# Revit family: Shower-Thermostat_Mixer-GROHE-Euphoria-26177_Series
name_source: partatom
category: Plumbing Fixtures
revit_build: Autodesk Revit 2014 (Build: 20130308_1515(x64)
units: mm (PartAtom-declared; Revit-internal decimal feet)

## types (2) — shared parameters
Assembly Code = D2010710
CW Connection = Yes
CWFU = 3
Cold Water Connection Diameter = 1/2"
Default Elevation = 40"
Description = EUPHORIA SYSTEM 260 Shower System with Bath Thermostat for Wall Mount
Finish = Metal-Grohe-000-Chrome
HW Connection = Yes
HWFU = 3
Height = 2 3/4"
Hot Water Connection Diameter = 1"
Installation Type = Wall Mounted
Manufacturer = Grohe
Material = Metal-Grohe-000-Chrome
Price = Prices may vary. Please consult Manufacturer Representative for most up-to-date price list.
Product Page URL = https://www.grohe.ca
Tempered Connection Diameter = 1/2"
URL = https://www.grohe.us
Vent Connection = No
WFU = 4
Warranty Documentation Link = https://cdn.cloud.grohe.com
Waste Connection = No
Width = 11 3/4"

## type names (no varying parameters)
- 26177001
- 26177000

note: column(s) folded — value = type name in every type: Model

## geometry (parser evidence)
native form markers: Sweep x4
no freeform markers — native parametric forms only
